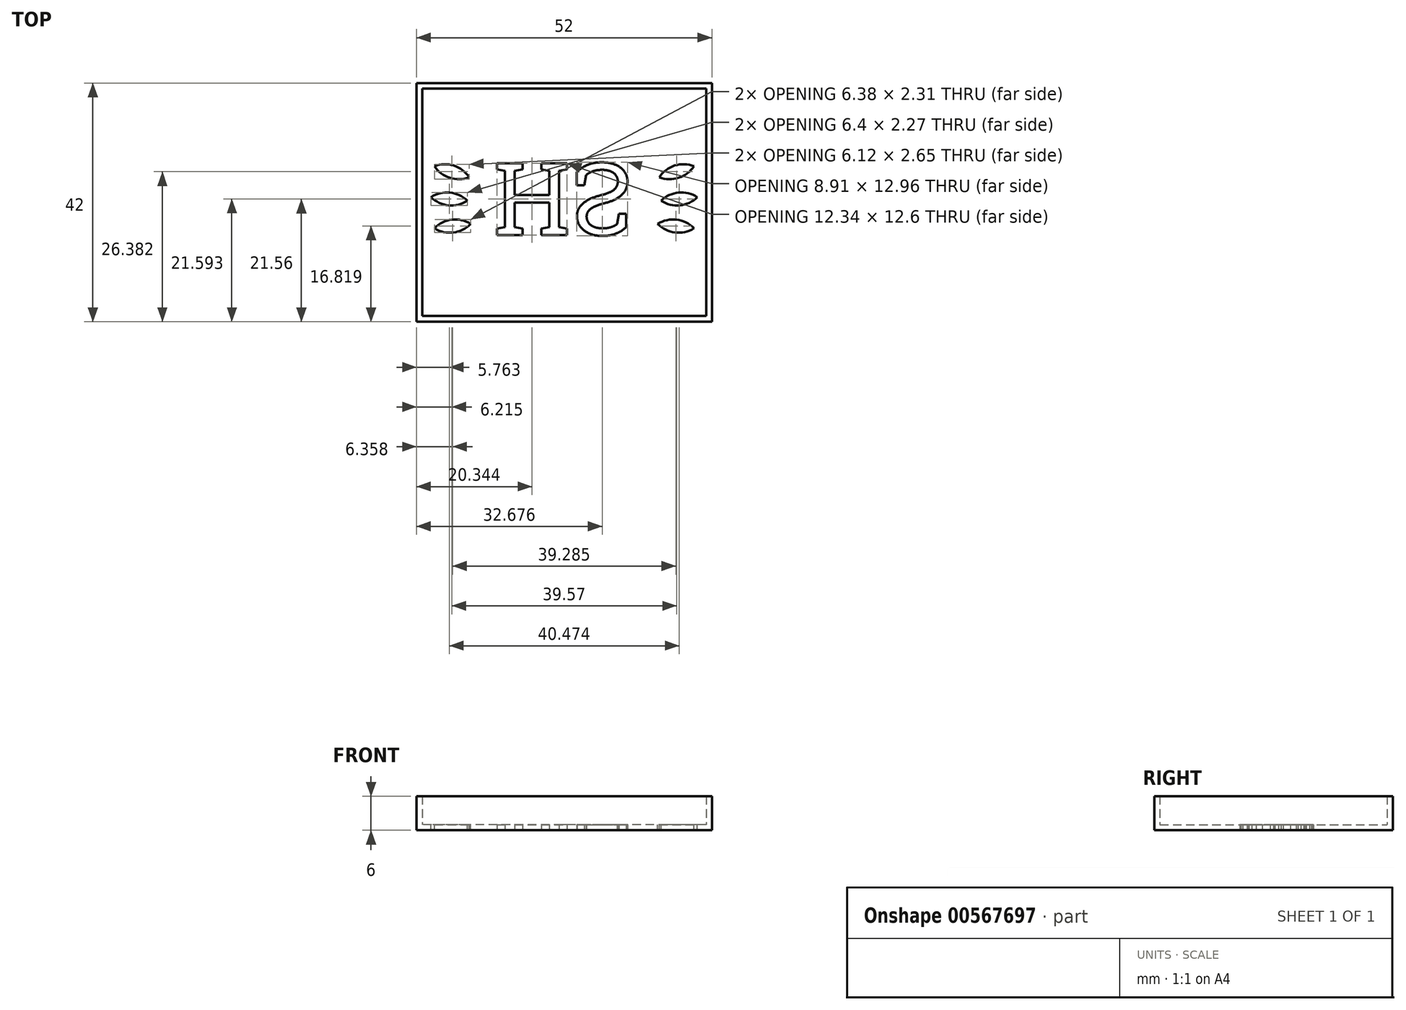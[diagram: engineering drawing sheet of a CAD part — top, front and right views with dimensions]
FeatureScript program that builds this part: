
annotation { "Feature Type Name" : "Feature", "Feature Type Description" : "" }
export const myFeature = defineFeature(function(context is Context, id is Id, definition is map)
    precondition{}
    {
        {
            var Q0;
            Q0=qCreatedBy(makeId("Top.planeOp"),FACE);
            var sketch = newSketch(context, id + "F0", { "sketchPlane" : qUnion([Q0])});
            skArc(sketch, "E0", {"start": v(-22.83, -4.57) * mm, "mid": v(-19.5, -5.3) * mm, "end": v(-16.45, -3.79) * mm});
            skLineSegment(sketch, "E1", {"start": v(-22.83, -4.57) * mm, "end": v(-16.45, -3.79) * mm, "construction": true});
            skArc(sketch, "E2.MirrorCS", {"start": v(-22.83, -4.57) * mm, "mid": v(-19.78, -3.06) * mm, "end": v(-16.45, -3.79) * mm});
            skArc(sketch, "E3.1.0", {"start": v(-23.44, 0.9) * mm, "mid": v(-20.13, 1.72) * mm, "end": v(-17.04, 0.28) * mm});
            skLineSegment(sketch, "E3.1.1", {"start": v(-23.44, 0.9) * mm, "end": v(-17.04, 0.28) * mm, "construction": true});
            skArc(sketch, "E3.1.2", {"start": v(-23.44, 0.9) * mm, "mid": v(-20.35, -0.53) * mm, "end": v(-17.04, 0.28) * mm});
            skArc(sketch, "E3.2.0", {"start": v(-22.84, 6.38) * mm, "mid": v(-19.44, 6.46) * mm, "end": v(-16.73, 4.39) * mm});
            skLineSegment(sketch, "E3.2.1", {"start": v(-22.84, 6.38) * mm, "end": v(-16.73, 4.39) * mm, "construction": true});
            skArc(sketch, "E3.2.2", {"start": v(-22.84, 6.38) * mm, "mid": v(-20.13, 4.3) * mm, "end": v(-16.73, 4.39) * mm});
            skLineSegment(sketch, "E3.anchor1", {"start": v(-5.46, 0) * mm, "end": v(-27.34, 6.72) * mm, "construction": true});
            skLineSegment(sketch, "E3.anchor2", {"start": v(-5.46, 0) * mm, "end": v(-22.45, 15.34) * mm, "construction": true});
            skLineSegment(sketch, "E4", {"start": v(0, 28.32) * mm, "end": v(0, -18.03) * mm, "construction": true});
            skLineSegment(sketch, "E5.MirrorCS", {"start": v(23.44, 0.9) * mm, "end": v(17.04, 0.28) * mm, "construction": true});
            skArc(sketch, "E6.MirrorCS", {"start": v(23.44, 0.9) * mm, "mid": v(20.13, 1.72) * mm, "end": v(17.04, 0.28) * mm});
            skArc(sketch, "E7.MirrorCS", {"start": v(22.83, -4.57) * mm, "mid": v(19.78, -3.06) * mm, "end": v(16.45, -3.79) * mm});
            skLineSegment(sketch, "E8.MirrorCS", {"start": v(22.84, 6.38) * mm, "end": v(16.73, 4.39) * mm, "construction": true});
            skLineSegment(sketch, "E9.MirrorCS", {"start": v(22.83, -4.57) * mm, "end": v(16.45, -3.79) * mm, "construction": true});
            skArc(sketch, "E10.MirrorCS", {"start": v(22.83, -4.57) * mm, "mid": v(19.5, -5.3) * mm, "end": v(16.45, -3.79) * mm});
            skArc(sketch, "E11.MirrorCS", {"start": v(22.84, 6.38) * mm, "mid": v(20.13, 4.3) * mm, "end": v(16.73, 4.39) * mm});
            skArc(sketch, "E12.MirrorCS", {"start": v(22.84, 6.38) * mm, "mid": v(19.44, 6.46) * mm, "end": v(16.73, 4.39) * mm});
            skArc(sketch, "E13.MirrorCS", {"start": v(23.44, 0.9) * mm, "mid": v(20.35, -0.53) * mm, "end": v(17.04, 0.28) * mm});
            skPoint(sketch, "E14.middle", {"position": v(-5.46, 0) * mm});
            skLineSegment(sketch, "E15.bottom", {"start": v(26, -21) * mm, "end": v(-26, -21) * mm});
            skLineSegment(sketch, "E15.top", {"start": v(26, 21) * mm, "end": v(-26, 21) * mm});
            skLineSegment(sketch, "E15.left", {"start": v(26, -21) * mm, "end": v(26, 21) * mm});
            skLineSegment(sketch, "E15.right", {"start": v(-26, -21) * mm, "end": v(-26, 21) * mm});
            skPoint(sketch, "E15.middle", {"position": v(0, 0) * mm});
            skSolve(sketch);
        }
        {
            var Q0;
            Q0=qCreatedBy(makeId("Top.planeOp"),FACE);
            var sketch = newSketch(context, id + "F1", { "sketchPlane" : qUnion([Q0])});
            skPoint(sketch, "E16.middle", {"position": v(0, 0) * mm});
            skLineSegment(sketch, "E17.bottom", {"start": v(26, -21) * mm, "end": v(-26, -21) * mm});
            skLineSegment(sketch, "E17.top", {"start": v(26, 21) * mm, "end": v(-26, 21) * mm});
            skLineSegment(sketch, "E17.left", {"start": v(26, -21) * mm, "end": v(26, 21) * mm});
            skLineSegment(sketch, "E17.right", {"start": v(-26, -21) * mm, "end": v(-26, 21) * mm});
            skLineSegment(sketch, "E18.0", {"start": v(25, 20) * mm, "end": v(-25, 20) * mm});
            skLineSegment(sketch, "E18.1", {"start": v(25, -20) * mm, "end": v(25, 20) * mm});
            skLineSegment(sketch, "E18.2", {"start": v(25, -20) * mm, "end": v(-25, -20) * mm});
            skLineSegment(sketch, "E18.3", {"start": v(-25, -20) * mm, "end": v(-25, 20) * mm});
            skSolve(sketch);
        }
        {
            var Q0;
            Q0=qSketchRegion(id+"F1",true);
            extrude(context, id + "F2", {"entities" : qUnion([Q0]), "depth" : 5 * mm, "offsetDistance" : 25 * mm});
        }
        {
            var Q0;
            Q0=qSketchRegion(id+"F0",true);
            extrude(context, id + "F3", {"entities" : qUnion([Q0]), "operationType" : NewBodyOperationType.ADD, "oppositeDirection" : true, "depth" : 1 * mm, "offsetDistance" : 25 * mm});
        }
        {
            var Q0;
            Q0=makeQuery(id+"F3.opExtrude","CAP_FACE",FACE,{"disambiguationData":[OSD([sQuery(id+"F0.wireOp",EDGE,"UQEWY4dh-ZNNd-hBIR-G8dA-HDRRqss2LeDl.bottom"),sQuery(id+"F0.wireOp",EDGE,"UQEWY4dh-ZNNd-hBIR-G8dA-HDRRqss2LeDl.top"),sQuery(id+"F0.wireOp",EDGE,"UQEWY4dh-ZNNd-hBIR-G8dA-HDRRqss2LeDl.left"),sQuery(id+"F0.wireOp",EDGE,"UQEWY4dh-ZNNd-hBIR-G8dA-HDRRqss2LeDl.right"),sQuery(id+"F0.wireOp",EDGE,"E0"),sQuery(id+"F0.wireOp",EDGE,"E2.MirrorCS"),sQuery(id+"F0.wireOp",EDGE,"E3.1.0"),sQuery(id+"F0.wireOp",EDGE,"E3.1.2"),sQuery(id+"F0.wireOp",EDGE,"E3.2.0"),sQuery(id+"F0.wireOp",EDGE,"E3.2.2"),sQuery(id+"F0.wireOp",EDGE,"E6.MirrorCS"),sQuery(id+"F0.wireOp",EDGE,"E7.MirrorCS"),sQuery(id+"F0.wireOp",EDGE,"E10.MirrorCS"),sQuery(id+"F0.wireOp",EDGE,"E11.MirrorCS"),sQuery(id+"F0.wireOp",EDGE,"E12.MirrorCS"),sQuery(id+"F0.wireOp",EDGE,"E13.MirrorCS")])],"isStart":false});
            var sketch = newSketch(context, id + "F4", { "sketchPlane" : qUnion([Q0])});
            skPoint(sketch, "E19.middle", {"position": v(-0.01, 0.08) * mm});
            skText(sketch, "E20", { "text": "HS", "fontName": "RobotoSlab-Regular.ttf"});
            const initialGuessF4  = {"E20": [-0.01244, -0.00686, 1, 0, 0.01276]};
            skSetInitialGuess(sketch, initialGuessF4);
            skSolve(sketch);
        }
        {
            var Q0;
            Q0 = qSketchRegion(id + "F4", true);
            extrude(context, id + "F5", {"entities" : qUnion([Q0]), "operationType" : NewBodyOperationType.REMOVE, "oppositeDirection" : true, "depth" : 3 * mm, "offsetDistance" : 25 * mm});
        }
    });
